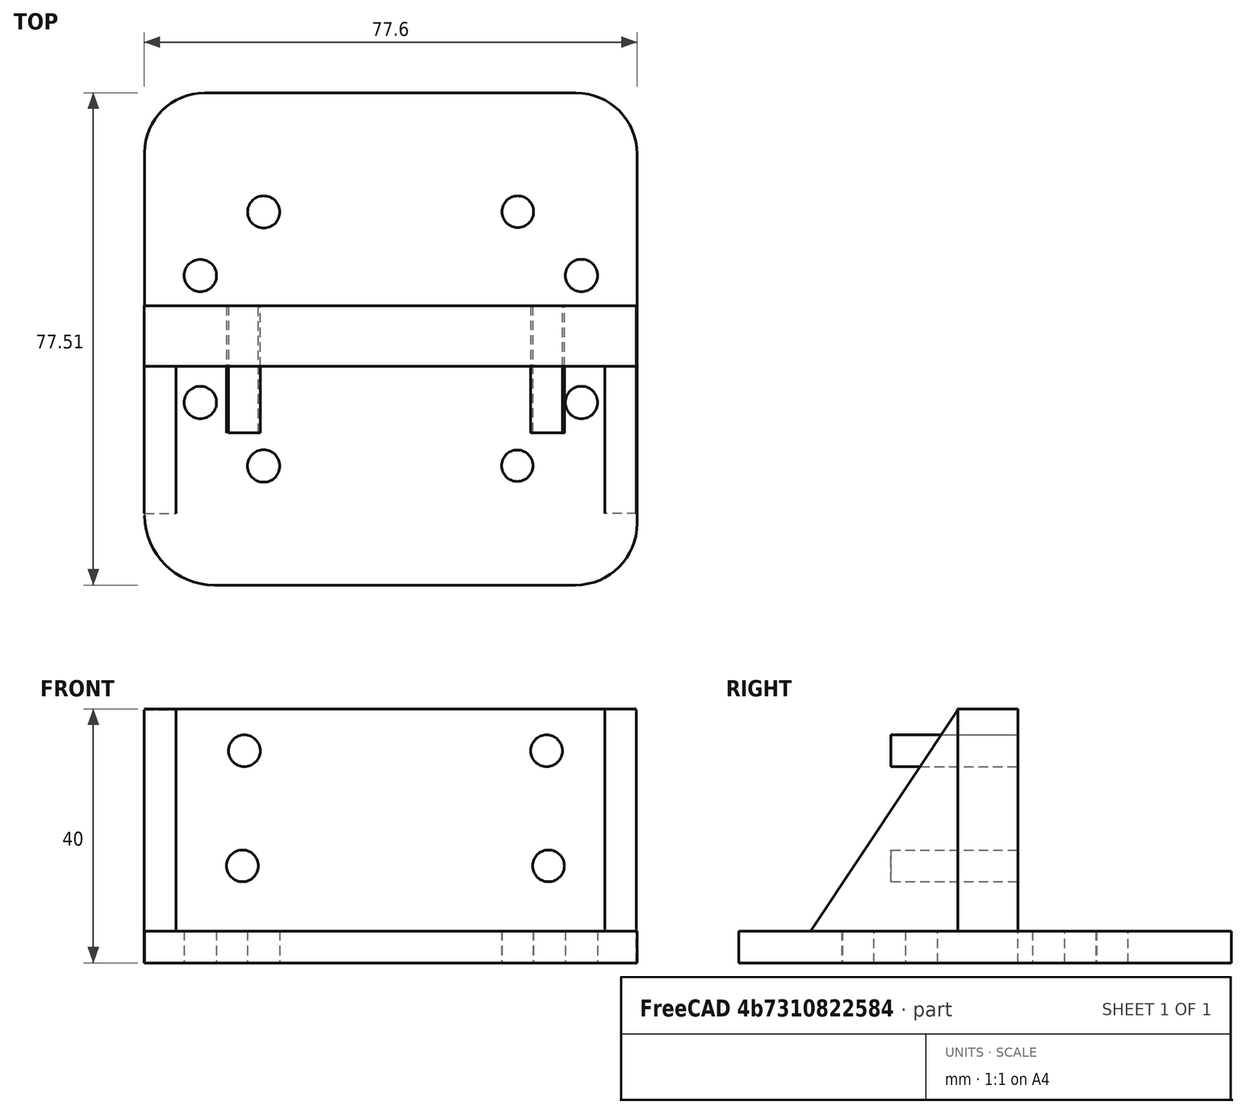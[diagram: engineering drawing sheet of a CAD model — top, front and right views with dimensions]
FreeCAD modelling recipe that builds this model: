
FCSTD DOCUMENT  (FreeCAD 0.14R2935 (Git))
Label: C-beam gantry plate bracket adapter 2
License: CC-BY 3.0
LicenseURL: http://creativecommons.org/licenses/by/3.0/
objects: Sketcher::SketchObject×5, PartDesign::Pad×4, Mesh::Feature×1, PartDesign::Pocket×1
note: 15 computed .brp shape members not serialized (recipe doc carries the construction recipe); baked Part::Feature solids carry a one-line shape summary decoded from their .brp

FEATURE [Mesh::Feature] C_Beam_Gantry_Plate_V1_STL  label="C-Beam_Gantry Plate_V1_STL"
FEATURE [Sketcher::SketchObject] Sketch
  Placement = pos=(77.6,0,0) rot=(0,0,1;1.5708rad)
  sketch-geometry (16):
    g0: LineSegment StartX=9.70494 StartY=0 StartZ=0 EndX=67.8794 EndY=0 EndZ=0
    g1: LineSegment StartX=77.51 StartY=9.6306 StartZ=0 EndX=77.51 EndY=68.0986 EndZ=0
    g2: LineSegment StartX=68.0986 StartY=77.51 StartZ=0 EndX=10.9616 EndY=77.51 EndZ=0
    g3: LineSegment StartX=0 StartY=66.5484 StartZ=0 EndX=0 EndY=9.70494 EndZ=0
    g4: Circle CenterX=28.75 CenterY=68.75 CenterZ=0 NormalX=0 NormalY=0 NormalZ=1 Radius=2.55
    g5: Circle CenterX=48.75 CenterY=68.75 CenterZ=0 NormalX=0 NormalY=0 NormalZ=1 Radius=2.55
    g6: Circle CenterX=48.76 CenterY=8.76 CenterZ=0 NormalX=0 NormalY=0 NormalZ=1 Radius=2.55
    g7: Circle CenterX=28.76 CenterY=8.76 CenterZ=0 NormalX=0 NormalY=0 NormalZ=1 Radius=2.55
    g8: Circle CenterX=18.755 CenterY=58.7909 CenterZ=0 NormalX=0 NormalY=0 NormalZ=1 Radius=2.55
    g9: Circle CenterX=58.755 CenterY=58.7765 CenterZ=0 NormalX=0 NormalY=0 NormalZ=1 Radius=2.53802
    g10: Circle CenterX=58.7985 CenterY=18.7777 CenterZ=0 NormalX=0 NormalY=0 NormalZ=1 Radius=2.49102
    g11: Circle CenterX=18.7993 CenterY=18.8618 CenterZ=0 NormalX=0 NormalY=0 NormalZ=1 Radius=2.47518
    g12: ArcOfCircle CenterX=10.9616 CenterY=66.5484 CenterZ=0 NormalX=0 NormalY=0 NormalZ=1 Radius=10.9616 StartAngle=1.5708 EndAngle=3.14159
    g13: ArcOfCircle CenterX=68.0986 CenterY=68.0986 CenterZ=0 NormalX=0 NormalY=0 NormalZ=1 Radius=9.41137 StartAngle=0 EndAngle=1.5708
    g14: ArcOfCircle CenterX=67.8794 CenterY=9.6306 CenterZ=0 NormalX=0 NormalY=0 NormalZ=1 Radius=9.6306 StartAngle=4.71239 EndAngle=6.28319
    g15: ArcOfCircle CenterX=9.70494 CenterY=9.70494 CenterZ=0 NormalX=0 NormalY=0 NormalZ=1 Radius=9.70494 StartAngle=3.14159 EndAngle=4.71239
  constraints (8):
    c: Tangent(g2,g12) = -1.5708
    c: Tangent(g3,g12) = -1.5708
    c: Tangent(g1,g13) = -1.5708
    c: Tangent(g2,g13) = -1.5708
    c: Tangent(g0,g14) = -1.5708
    c: Tangent(g1,g14) = -1.5708
    c: Tangent(g0,g15) = -1.5708
    c: Tangent(g3,g15) = -1.5708
FEATURE [PartDesign::Pad] Pad
  Length = 5
  Length2 = 100
  Placement = pos=(77.6,0,0) rot=(0,0,1;1.5708rad)
  Sketch = -> Sketch
  Type = 0
FEATURE [Sketcher::SketchObject] Sketch001
  sketch-geometry (4):
    g0: LineSegment StartX=0 StartY=43.9597 StartZ=0 EndX=77.4599 EndY=43.9597 EndZ=0
    g1: LineSegment StartX=77.4599 StartY=43.9597 StartZ=0 EndX=77.4599 EndY=34.4451 EndZ=0
    g2: LineSegment StartX=77.4599 StartY=34.4451 StartZ=0 EndX=0 EndY=34.4451 EndZ=0
    g3: LineSegment StartX=0 StartY=34.4451 StartZ=0 EndX=0 EndY=43.9597 EndZ=0
  constraints (9):
    c: Coincident(g0,g1)
    c: Coincident(g1,g2)
    c: Coincident(g2,g3)
    c: Coincident(g3,g0)
    c: Horizontal(g0)
    c: Horizontal(g2)
    c: Vertical(g1)
    c: Vertical(g3)
    c: PointOnObject(g0,g-2)
FEATURE [PartDesign::Pad] Pad001
  Length = 40
  Length2 = 100
  Sketch = -> Sketch001
  Type = 0
FEATURE [Sketcher::SketchObject] Sketch002
  Placement = pos=(0,43.9597,0) rot=(0,0.707107,0.707107;3.14159rad)
  Support = -> Pad001 [Face1]
  sketch-geometry (4):
    g0: Circle CenterX=-15.7771 CenterY=33.4012 CenterZ=0 NormalX=0 NormalY=0 NormalZ=1 Radius=2.5
    g1: Circle CenterX=-15.4766 CenterY=15.2734 CenterZ=0 NormalX=0 NormalY=0 NormalZ=1 Radius=2.5
    g2: Circle CenterX=-63.35 CenterY=33.4012 CenterZ=0 NormalX=0 NormalY=0 NormalZ=1 Radius=2.5
    g3: Circle CenterX=-63.6505 CenterY=15.2734 CenterZ=0 NormalX=0 NormalY=0 NormalZ=1 Radius=2.5
  constraints (6):
    c: Radius(g2) = 2.5
    c: Radius(g3) = 2.5
    c: Radius(g0) = 2.5
    c: Radius(g1) = 2.5
    c: DistanceY(g0,g2) = 0
    c: DistanceY(g3,g1) = 0
FEATURE [PartDesign::Pocket] Pocket
  Length = 20
  Sketch = -> Sketch002
  Type = 0
FEATURE [Sketcher::SketchObject] Sketch003
  Placement = pos=(0,0.02,0) rot=(0.57735,0.57735,0.57735;2.0944rad)
  sketch-geometry (3):
    g0: LineSegment StartX=11.2585 StartY=4.91979 StartZ=0 EndX=34.4402 EndY=39.8674 EndZ=0
    g1: LineSegment StartX=34.4402 StartY=39.8674 StartZ=0 EndX=34.4402 EndY=4.91979 EndZ=0
    g2: LineSegment StartX=34.4402 StartY=4.91979 StartZ=0 EndX=11.2585 EndY=4.91979 EndZ=0
  constraints (5):
    c: Coincident(g0,g1)
    c: Vertical(g1)
    c: Coincident(g1,g2)
    c: Coincident(g2,g0)
    c: Horizontal(g2)
FEATURE [PartDesign::Pad] Pad002
  Length = 5
  Length2 = 100
  Placement = pos=(0,0.02,0) rot=(0.57735,0.57735,0.57735;2.0944rad)
  Sketch = -> Sketch003
  Type = 0
FEATURE [Sketcher::SketchObject] Sketch004
  Placement = pos=(77.5,0.02,0) rot=(0.57735,0.57735,0.57735;2.0944rad)
  sketch-geometry (3):
    g0: LineSegment StartX=11.2585 StartY=4.91979 StartZ=0 EndX=34.4402 EndY=39.8674 EndZ=0
    g1: LineSegment StartX=34.4402 StartY=39.8674 StartZ=0 EndX=34.4402 EndY=4.91979 EndZ=0
    g2: LineSegment StartX=34.4402 StartY=4.91979 StartZ=0 EndX=11.2585 EndY=4.91979 EndZ=0
  constraints (5):
    c: Coincident(g0,g1)
    c: Vertical(g1)
    c: Coincident(g1,g2)
    c: Coincident(g2,g0)
    c: Horizontal(g2)
FEATURE [PartDesign::Pad] Pad003
  Length = 5
  Length2 = 100
  Placement = pos=(77.5,0.02,0) rot=(0.57735,0.57735,0.57735;2.0944rad)
  Reversed = true
  Sketch = -> Sketch004
  Type = 0
